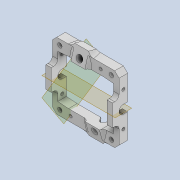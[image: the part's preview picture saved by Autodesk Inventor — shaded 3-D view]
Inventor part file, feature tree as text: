
AUTODESK INVENTOR PART (.ipt)
format: ipt  version: 2020 (Build 240168000, 168)  size: 724,480 bytes
history: native  units: mm
features: reference x17, projected_geometry x17, extrude x15, sketch x15, other x7, fillet x5, plane x4, thicken_offset x4, chamfer x3, mirror x2
ambient origin geometry x8: Origin, YZ Plane, XZ Plane, XY Plane, X Axis, Y Axis, Z Axis, Center Point
bodies: Solid1 (feature_tree)
feature tree (89):
  extrude  "Extrusion1"  Depth=21.0mm
  extrude  "Extrusion2"  Depth=2.5mm
  extrude  "Extrusion3"  Depth=4.0mm TaperAngle=0.0deg
  extrude  "Extrusion4"  Depth=10.0mm TaperAngle=0.0deg
  extrude  "Extrusion5"  Depth=10.0mm TaperAngle=0.0deg
  extrude  "Extrusion6"  Depth=4.0mm
  extrude  "Extrusion7"  Depth=10.0mm
  plane  "Work Plane1"
  sketch  "Sketch8"  dims[d19=10.0mm d20=50.0mm d21=0.0mm]
  plane  "Work Plane2"
  extrude  "Extrusion8"  Depth=10.0mm TaperAngle=0.0deg
  plane  "Work Plane3"
  mirror  "Mirror1"
  extrude  "Extrusion9"  Depth=14.0mm
  sketch  "Sketch10"  dims[d25=12.0mm d26=50.0mm d27=0.0mm]
  plane  "Work Plane4"
  extrude  "Extrusion11"  Depth=50.0mm TaperAngle=0.0deg
  mirror  "Mirror2"
  extrude  "Extrusion12"  Depth=24.0mm
  chamfer  "Chamfer1"  Distance=5.0mm
  fillet  "Fillet1"  Radius=5.0mm
  extrude  "Extrusion13"  Depth=2.0mm
  chamfer  "Chamfer2"  Distance=5.0mm
  fillet  "Fillet2"  Radius=0.4mm
  thicken_offset  "Thicken1"
  thicken_offset  "Thicken2"
  thicken_offset  "Thicken3"
  thicken_offset  "Thicken4"
  extrude  "Extrusion14"  Depth=2.0mm TaperAngle=0.0deg
  extrude  "Extrusion15"  Depth=2.5mm
  fillet  "Fillet3"  Radius=3.85mm
  fillet  "Fillet4"  Radius=2.5mm
  extrude  "Extrusion16"  Depth=3.0mm
  chamfer  "Chamfer3"  Distance=7.0mm
  fillet  "Fillet5"  Radius=2.0mm
  sketch  "Sketch1"  dims[d0=26.0mm d1=21.0mm]
  reference  "Reference1"
  reference  "Reference2"
  reference  "Reference3"
  reference  "Reference4"
  reference  "Reference5"
  reference  "Reference6"
  reference  "Reference7"
  reference  "Reference8"
  sketch  "Sketch2"  dims[d2=5.0mm d3=2.5mm]
  reference  "Reference9"
  reference  "Reference10"
  sketch  "Sketch3"  dims[d4=4.0mm d5=0.0mm d6=4.0mm d7=0.0mm]
  projected_geometry  "Projected Loop1"
  reference  "Reference11"
  sketch  "Sketch4"  dims[d8=10.0mm d9=4.0mm d10=0.0mm]
  reference  "Reference12"
  sketch  "Sketch5"  dims[d11=10.0mm d12=4.0mm d13=0.0mm]
  reference  "Reference13"
  sketch  "Sketch6"  dims[d14=5.0mm d15=4.0mm]
  projected_geometry  "Projected Loop2"
  sketch  "Sketch7"  dims[d16=50.0mm d17=0.0mm d18=10.0mm]
  projected_geometry  "Projected Loop3"
  projected_geometry  "Projected Loop4"
  projected_geometry  "Projected Loop5"
  reference  "Reference14"
  sketch  "Sketch9"  dims[d22=50.0mm d23=0.0mm d24=14.0mm]
  projected_geometry  "Projected Loop6"
  projected_geometry  "Projected Loop7"
  projected_geometry  "Projected Loop8"
  projected_geometry  "Projected Loop9"
  projected_geometry  "Projected Loop10"
  reference  "Reference15"
  projected_geometry  "Projected Loop11"
  sketch  "Sketch11"  dims[d28=26.0mm d29=24.0mm]
  reference  "Reference16"
  projected_geometry  "Projected Loop12"
  sketch  "Sketch12"  dims[d30=2.0mm]
  projected_geometry  "Projected Loop13"
  reference  "Reference17"
  sketch  "Sketch13"  dims[d31=2.0mm]
  projected_geometry  "Projected Loop14"
  sketch  "Sketch14"  dims[d32=2.0mm]
  projected_geometry  "Projected Loop15"
  sketch  "Sketch15"  dims[d33=2.0mm d34=5.0mm d35=0.0mm d37=5.0mm d38=0.4mm d39=5.0mm d42=0.4mm d43=4.0mm d44=0.0mm d45=2.5mm d46=3.85mm d47=2.5mm d48=3.0mm d49=7.0mm d50=0.0mm d51=0.5mm d52=2.0mm d53=45.0deg d54=0.2mm d55=2.5mm d56=3.85mm d57=3.0mm d58=7.0mm d59=0.0mm d60=0.5mm d61=2.0mm d62=45.0deg d63=0.2mm d64=8.25mm d65=9.0mm d66=6.0mm d67=6.0mm d68=1.5mm d69=1.5mm d70=0.75mm d71=0.75mm d72=6.5mm d73=1.5mm d74=7.0mm d75=0.0mm d76=6.5mm d77=1.5mm d78=7.0mm d79=0.0mm d80=3.0mm d81=2.0mm d82=5.0mm d83=5.0mm d84=1.4mm d85=1.4mm d86=7.0mm d87=0.0mm d88=2.0mm d89=2.0mm d90=45.0deg d91=2.0mm]
  projected_geometry  "Projected Loop16"
  projected_geometry  "Projected Loop17"
  parser-record x1  (decoder bookkeeping rows leaked as tree rows — omitted from the tree; the rows remain in map.json)
  other  "tip_3_n_ass.iam"
  other  "bearing_hh_1:2"
  other  "bearing_hh_1:1"
  other  "pin3_40:1"
  other  "roller_n_1:1"
  other  "roller_n_1:2"
note: 1 file-system path scrubbed to <path> (originals preserved in map.json)
